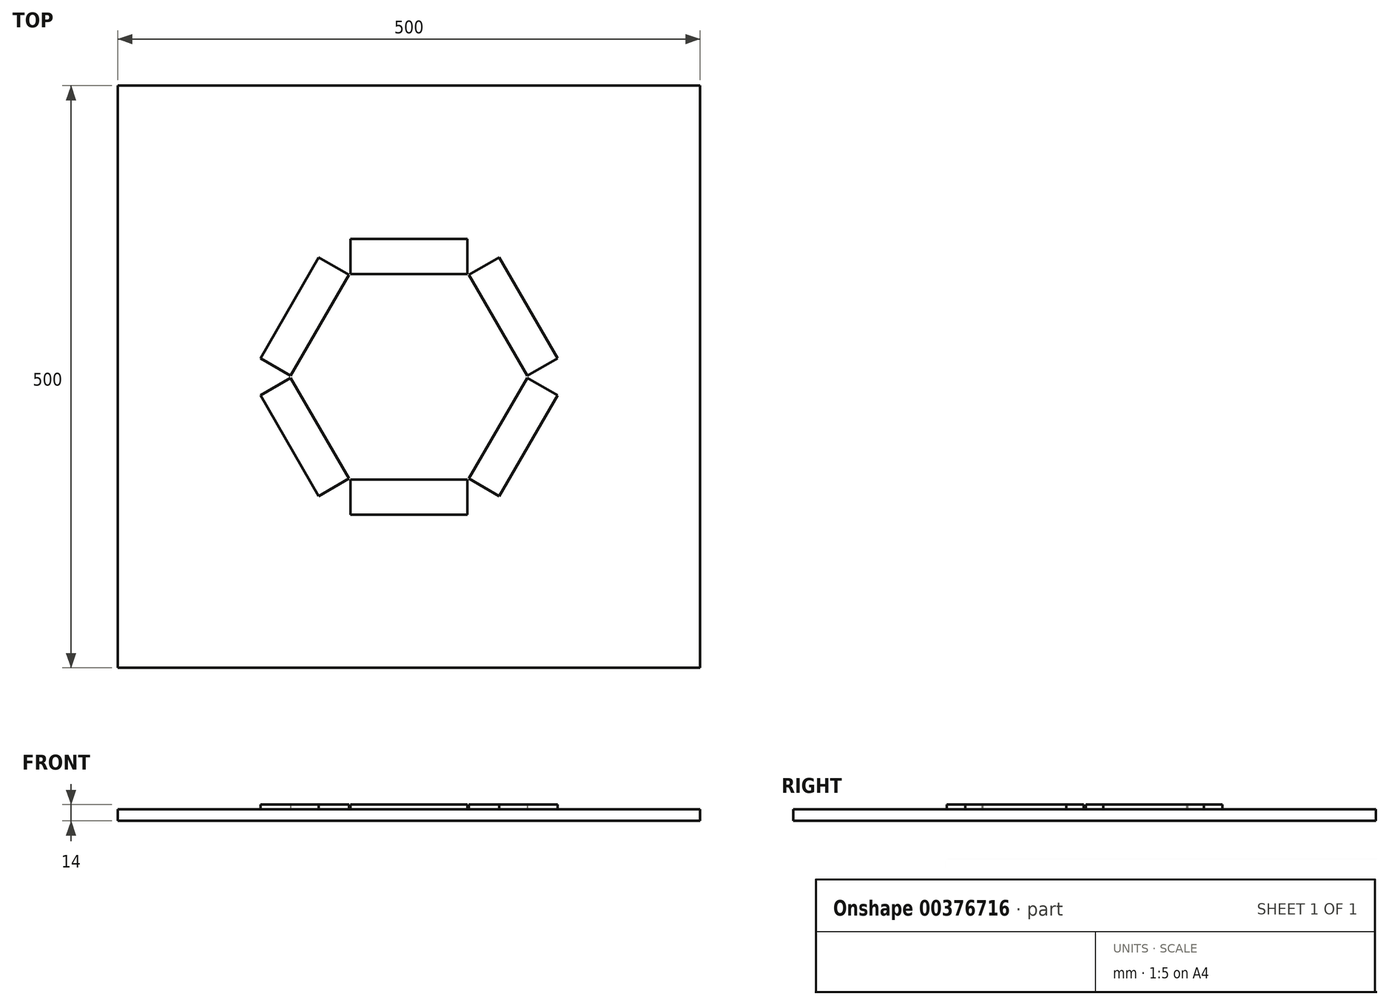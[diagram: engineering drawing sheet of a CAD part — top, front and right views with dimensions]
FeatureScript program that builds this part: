
annotation { "Feature Type Name" : "Feature", "Feature Type Description" : "" }
export const myFeature = defineFeature(function(context is Context, id is Id, definition is map)
    precondition{}
    {
        {
            var Q0;
            Q0=qCreatedBy(makeId("Top.planeOp"),FACE);
            var sketch = newSketch(context, id + "F0", { "sketchPlane" : qUnion([Q0])});
            skLineSegment(sketch, "E0.bottom", {"start": v(250, -250) * mm, "end": v(-250, -250) * mm});
            skLineSegment(sketch, "E0.top", {"start": v(250, 250) * mm, "end": v(-250, 250) * mm});
            skLineSegment(sketch, "E0.left", {"start": v(250, -250) * mm, "end": v(250, 250) * mm});
            skLineSegment(sketch, "E0.right", {"start": v(-250, -250) * mm, "end": v(-250, 250) * mm});
            skPoint(sketch, "E0.middle", {"position": v(0, 0) * mm});
            skSolve(sketch);
        }
        {
            var Q0;
            Q0 = qSketchRegion(id + "F0", true);
            extrude(context, id + "F1", {"entities" : qUnion([Q0]), "depth" : 10 * mm, "offsetDistance" : 25 * mm});
        }
        {
            var Q0;
            Q0=makeQuery(id+"F1.opExtrude","CAP_FACE",FACE,{"disambiguationData":[OSD([sQuery(id+"F0.wireOp",EDGE,"E0.bottom"),sQuery(id+"F0.wireOp",EDGE,"E0.top"),sQuery(id+"F0.wireOp",EDGE,"E0.left"),sQuery(id+"F0.wireOp",EDGE,"E0.right")])],"isStart":false});
            var sketch = newSketch(context, id + "F2", { "sketchPlane" : qUnion([Q0])});
            skCircle(sketch, "E1.cCircle", {"center": v(0, 0) * mm, "radius": 88.33 * mm, "construction": true});
            skLineSegment(sketch, "E1.0", {"start": v(51, -88.33) * mm, "end": v(-51, -88.33) * mm, "construction": true});
            skLineSegment(sketch, "E1.1", {"start": v(-51, -88.33) * mm, "end": v(-102, 0) * mm, "construction": true});
            skLineSegment(sketch, "E1.2", {"start": v(-102, 0) * mm, "end": v(-51, 88.33) * mm, "construction": true});
            skLineSegment(sketch, "E1.3", {"start": v(-51, 88.33) * mm, "end": v(51, 88.33) * mm, "construction": true});
            skLineSegment(sketch, "E1.4", {"start": v(51, 88.33) * mm, "end": v(102, 0) * mm, "construction": true});
            skLineSegment(sketch, "E1.5", {"start": v(102, 0) * mm, "end": v(51, -88.33) * mm, "construction": true});
            skPoint(sketch, "E1.0.midPoint", {"position": v(0, -88.33) * mm});
            skLineSegment(sketch, "E2.bottom", {"start": v(-50, 88.33) * mm, "end": v(50, 88.33) * mm});
            skLineSegment(sketch, "E2.top", {"start": v(-50, 118.33) * mm, "end": v(50, 118.33) * mm});
            skLineSegment(sketch, "E2.left", {"start": v(-50, 88.33) * mm, "end": v(-50, 118.33) * mm});
            skLineSegment(sketch, "E2.right", {"start": v(50, 88.33) * mm, "end": v(50, 118.33) * mm});
            skLineSegment(sketch, "E3.1.0", {"start": v(-127.48, 15.87) * mm, "end": v(-77.48, 102.47) * mm});
            skLineSegment(sketch, "E3.1.1", {"start": v(-101.5, 0.87) * mm, "end": v(-127.48, 15.87) * mm});
            skLineSegment(sketch, "E3.1.2", {"start": v(-51.5, 87.47) * mm, "end": v(-77.48, 102.47) * mm});
            skLineSegment(sketch, "E3.1.4", {"start": v(-101.5, 0.87) * mm, "end": v(-51.5, 87.47) * mm});
            skLineSegment(sketch, "E3.2.0", {"start": v(-77.48, -102.47) * mm, "end": v(-127.48, -15.87) * mm});
            skLineSegment(sketch, "E3.2.1", {"start": v(-51.5, -87.47) * mm, "end": v(-77.48, -102.47) * mm});
            skLineSegment(sketch, "E3.2.2", {"start": v(-101.5, -0.87) * mm, "end": v(-127.48, -15.87) * mm});
            skLineSegment(sketch, "E3.2.4", {"start": v(-51.5, -87.47) * mm, "end": v(-101.5, -0.87) * mm});
            skLineSegment(sketch, "E3.3.0", {"start": v(50, -118.33) * mm, "end": v(-50, -118.33) * mm});
            skLineSegment(sketch, "E3.3.1", {"start": v(50, -88.33) * mm, "end": v(50, -118.33) * mm});
            skLineSegment(sketch, "E3.3.2", {"start": v(-50, -88.33) * mm, "end": v(-50, -118.33) * mm});
            skLineSegment(sketch, "E3.3.4", {"start": v(50, -88.33) * mm, "end": v(-50, -88.33) * mm});
            skLineSegment(sketch, "E3.4.0", {"start": v(127.48, -15.87) * mm, "end": v(77.48, -102.47) * mm});
            skLineSegment(sketch, "E3.4.1", {"start": v(101.5, -0.87) * mm, "end": v(127.48, -15.87) * mm});
            skLineSegment(sketch, "E3.4.2", {"start": v(51.5, -87.47) * mm, "end": v(77.48, -102.47) * mm});
            skLineSegment(sketch, "E3.4.4", {"start": v(101.5, -0.87) * mm, "end": v(51.5, -87.47) * mm});
            skLineSegment(sketch, "E3.5.0", {"start": v(77.48, 102.47) * mm, "end": v(127.48, 15.87) * mm});
            skLineSegment(sketch, "E3.5.1", {"start": v(51.5, 87.47) * mm, "end": v(77.48, 102.47) * mm});
            skLineSegment(sketch, "E3.5.2", {"start": v(101.5, 0.87) * mm, "end": v(127.48, 15.87) * mm});
            skLineSegment(sketch, "E3.5.4", {"start": v(51.5, 87.47) * mm, "end": v(101.5, 0.87) * mm});
            skSolve(sketch);
        }
        {
            var Q0;
            Q0 = qSketchRegion(id + "F2", true);
            extrude(context, id + "F3", {"entities" : qUnion([Q0]), "operationType" : NewBodyOperationType.ADD, "depth" : 4 * mm, "offsetDistance" : 25 * mm});
        }
    });
